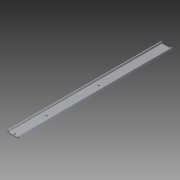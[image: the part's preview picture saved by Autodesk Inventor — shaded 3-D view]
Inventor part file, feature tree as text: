
AUTODESK INVENTOR PART (.ipt)
format: ipt  version: 2011 (Build 150239000, 239)  size: 131,584 bytes
history: native  units: in
note: dims shown in document units (in); Inventor stores cm internally (conversion verified against a paired STEP export)
features: extrude x6, sketch x6
ambient origin geometry x8: Origin, YZ Plane, XZ Plane, XY Plane, X Axis, Y Axis, Z Axis, Center Point
bodies: Solid1 (feature_tree)
feature tree (12):
  extrude  "Extrusion1"  Depth=0.374in
  extrude  "Extrusion2"  Depth=17.5197in TaperAngle=0.0deg
  extrude  "Extrusion3"  Depth=0.1693in
  extrude  "Extrusion4"  Depth=15.1181in
  extrude  "Extrusion5"  Depth=16.5in TaperAngle=0.0deg
  extrude  "Extrusion6"  Depth=3.585in
  sketch  "Sketch1"  dims[d0=1.3898in d1=0.374in]
  sketch  "Sketch2"  dims[d2=135.0deg d3=17.5197in d4=0.0in]
  sketch  "Sketch3"  dims[d5=1.1142in d6=0.1693in]
  sketch  "Sketch4"  dims[d7=13.8583in d8=15.1181in]
  sketch  "Sketch5"  dims[d9=17.5197in d10=0.0in d11=16.5in d12=0.0in]
  sketch  "Sketch6"  dims[d13=16.625in d14=0.0in d15=3.585in d16=0.185in d17=9.25in d18=16.625in d19=0.0in d20=0.175in d21=16.625in d22=0.0in]
